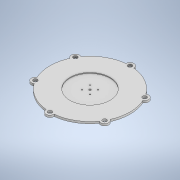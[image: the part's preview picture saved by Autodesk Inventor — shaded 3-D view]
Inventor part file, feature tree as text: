
AUTODESK INVENTOR PART (.ipt)
format: ipt  version: 2022 (Build 260153000, 153)  size: 165,376 bytes
history: native  units: mm
features: extrude x3, sketch x3
ambient origin geometry x8: Origin, YZ Plane, XZ Plane, XY Plane, X Axis, Y Axis, Z Axis, Center Point
bodies: Solid1 (feature_tree)
feature tree (6):
  extrude  "Extrusion1"  Depth=20.0mm
  extrude  "Extrusion2"  Depth=20.0mm
  extrude  "Extrusion3"  Depth=5.0mm
  sketch  "Sketch1"  dims[d0=200.0mm d3=20.0mm]
  sketch  "Sketch2"  dims[d4=20.0mm d5=20.0mm]
  sketch  "Sketch3"  dims[d6=20.0mm d7=20.0mm d8=20.0mm d9=10.0mm d10=10.0mm d11=10.0mm d12=10.0mm d13=10.0mm d14=10.0mm d15=5.0mm d16=0.0mm d17=100.0mm d18=2.0mm d19=0.0mm d20=5.0mm d29=3.0mm d30=3.0mm d31=3.0mm d32=3.0mm d33=5.0mm d34=0.0mm]
